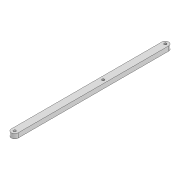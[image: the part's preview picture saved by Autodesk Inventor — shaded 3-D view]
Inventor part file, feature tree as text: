
AUTODESK INVENTOR PART (.ipt)
format: ipt  version: 2022 (Build 260153000, 153)  size: 89,600 bytes
history: native  units: mm
features: extrude x1, sketch x1
ambient origin geometry x8: Origin, YZ Plane, XZ Plane, XY Plane, X Axis, Y Axis, Z Axis, Center Point
bodies: Solid1 (feature_tree)
feature tree (2):
  extrude  "Extrusion1"  Depth=4.0mm
  sketch  "Sketch1"  dims[d0=2.2mm d1=2.2mm d2=6.0mm d3=132.469mm d4=2.2mm d5=77.759mm d6=4.0mm d7=0.0mm]
